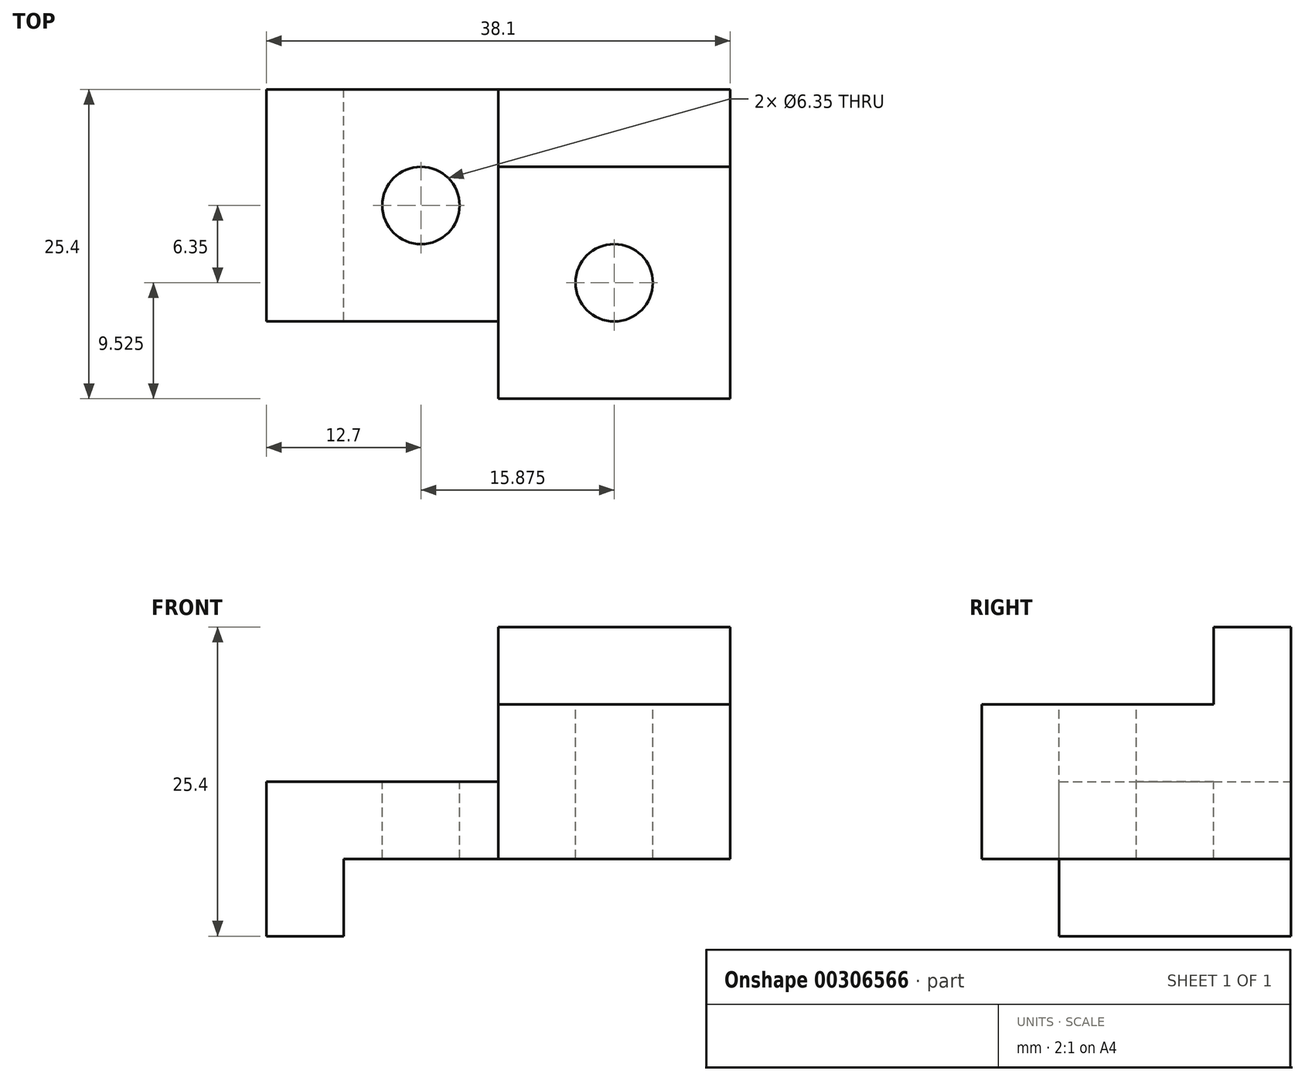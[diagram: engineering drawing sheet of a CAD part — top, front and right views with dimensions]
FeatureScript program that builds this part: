
annotation { "Feature Type Name" : "Feature", "Feature Type Description" : "" }
export const myFeature = defineFeature(function(context is Context, id is Id, definition is map)
    precondition{}
    {
        {
            var Q0;
            Q0=qCreatedBy(makeId("Front.planeOp"),FACE);
            var sketch = newSketch(context, id + "F0", { "sketchPlane" : qUnion([Q0])});
            skLineSegment(sketch, "E0", {"start": v(0, 0) * mm, "end": v(19.05, 0) * mm});
            skLineSegment(sketch, "E1", {"start": v(19.05, 0) * mm, "end": v(19.05, 12.7) * mm});
            skLineSegment(sketch, "E2", {"start": v(19.05, 12.7) * mm, "end": v(38.1, 12.7) * mm});
            skLineSegment(sketch, "E3", {"start": v(38.1, 12.7) * mm, "end": v(38.1, -6.35) * mm});
            skLineSegment(sketch, "E4", {"start": v(38.1, -6.35) * mm, "end": v(6.35, -6.35) * mm});
            skLineSegment(sketch, "E5", {"start": v(6.35, -6.35) * mm, "end": v(6.35, -12.7) * mm});
            skLineSegment(sketch, "E6", {"start": v(6.35, -12.7) * mm, "end": v(0, -12.7) * mm});
            skLineSegment(sketch, "E7", {"start": v(0, -12.7) * mm, "end": v(0, 0) * mm});
            skSolve(sketch);
        }
        {
            var Q0;
            Q0 = qSketchRegion(id + "F0", true);
            extrude(context, id + "F1", {"entities" : qUnion([Q0]), "endBound" : BoundingType.SYMMETRIC, "depth" : 25.4 * mm});
        }
        {
            var Q0;
            Q0=makeQuery(id+"F1.opExtrude","SWEPT_FACE",FACE,{"disambiguationData":[OSD([sQuery(id+"F0.wireOp",EDGE,"E3")])]});
            var sketch = newSketch(context, id + "F2", { "sketchPlane" : qUnion([Q0])});
            skLineSegment(sketch, "E8", {"start": v(-12.7, 12.7) * mm, "end": v(6.35, 12.7) * mm});
            skLineSegment(sketch, "E9", {"start": v(6.35, 12.7) * mm, "end": v(6.35, 6.35) * mm});
            skLineSegment(sketch, "E10", {"start": v(6.35, 6.35) * mm, "end": v(-12.7, 6.35) * mm});
            skLineSegment(sketch, "E11", {"start": v(-12.7, 6.35) * mm, "end": v(-12.7, 12.7) * mm});
            skSolve(sketch);
        }
        {
            var Q0;
            Q0 = qSketchRegion(id + "F2", true);
            extrude(context, id + "F3", {"entities" : qUnion([Q0]), "operationType" : NewBodyOperationType.REMOVE, "endBound" : BoundingType.THROUGH_ALL, "oppositeDirection" : true, "depth" : 25.4 * mm});
        }
        {
            var Q0;
            Q0=makeQuery(id+"F1.opExtrude","SWEPT_FACE",FACE,{"disambiguationData":[OSD([sQuery(id+"F0.wireOp",EDGE,"E5")])]});
            var sketch = newSketch(context, id + "F4", { "sketchPlane" : qUnion([Q0])});
            skLineSegment(sketch, "E12", {"start": v(-12.7, -6.35) * mm, "end": v(-6.35, -6.35) * mm});
            skLineSegment(sketch, "E13", {"start": v(-6.35, -6.35) * mm, "end": v(-6.35, -12.7) * mm});
            skLineSegment(sketch, "E14", {"start": v(-6.35, -12.7) * mm, "end": v(-12.7, -12.7) * mm});
            skLineSegment(sketch, "E15", {"start": v(-12.7, -12.7) * mm, "end": v(-12.7, -6.35) * mm});
            skSolve(sketch);
        }
        {
            var Q0;
            Q0 = qSketchRegion(id + "F4", true);
            extrude(context, id + "F5", {"entities" : qUnion([Q0]), "operationType" : NewBodyOperationType.REMOVE, "endBound" : BoundingType.THROUGH_ALL, "oppositeDirection" : true, "depth" : 25.4 * mm});
        }
        {
            var Q0;
            Q0=makeQuery(id+"F1.opExtrude","SWEPT_FACE",FACE,{"disambiguationData":[OSD([sQuery(id+"F0.wireOp",EDGE,"E0")])]});
            var sketch = newSketch(context, id + "F6", { "sketchPlane" : qUnion([Q0])});
            skLineSegment(sketch, "E16", {"start": v(0, -12.7) * mm, "end": v(19.05, -12.7) * mm});
            skLineSegment(sketch, "E17", {"start": v(19.05, -12.7) * mm, "end": v(19.05, -6.35) * mm});
            skLineSegment(sketch, "E18", {"start": v(19.05, -6.35) * mm, "end": v(0, -6.35) * mm});
            skLineSegment(sketch, "E19", {"start": v(0, -6.35) * mm, "end": v(0, -12.7) * mm});
            skCircle(sketch, "E20", {"center": v(12.7, 3.17) * mm, "radius": 3.18 * mm});
            skSolve(sketch);
        }
        {
            var Q0;
            Q0 = qSketchRegion(id + "F6", true);
            extrude(context, id + "F7", {"entities" : qUnion([Q0]), "operationType" : NewBodyOperationType.REMOVE, "endBound" : BoundingType.THROUGH_ALL, "oppositeDirection" : true, "depth" : 25.4 * mm});
        }
        {
            var Q0;
            Q0=makeQuery(id+"F3.boolean.opBoolean","COPY",FACE,{"derivedFrom":makeQuery(id+"F3.opExtrude","SWEPT_FACE",FACE,{"disambiguationData":[OSD([sQuery(id+"F2.wireOp",EDGE,"E10")])]})});
            var sketch = newSketch(context, id + "F8", { "sketchPlane" : qUnion([Q0])});
            skCircle(sketch, "E21", {"center": v(28.58, -3.17) * mm, "radius": 3.18 * mm});
            skPoint(sketch, "E21.centerSnap0", {"position": v(28.58, 6.35) * mm});
            skSolve(sketch);
        }
        {
            var Q0;
            Q0 = qSketchRegion(id + "F8", true);
            extrude(context, id + "F9", {"entities" : qUnion([Q0]), "operationType" : NewBodyOperationType.REMOVE, "endBound" : BoundingType.THROUGH_ALL, "oppositeDirection" : true, "depth" : 25.4 * mm});
        }
    });
